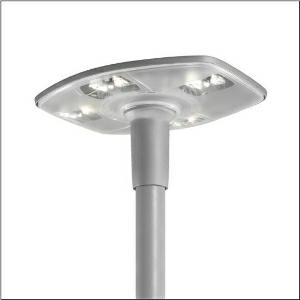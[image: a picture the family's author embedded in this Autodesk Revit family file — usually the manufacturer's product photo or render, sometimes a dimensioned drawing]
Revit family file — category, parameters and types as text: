
# Revit family: dl_r__30_led___st1_2c_5xa513271b08a5_992b
name_source: partatom
category: Lighting Fixtures
units: mm (PartAtom-declared; Revit-internal decimal feet)

## family parameters
Cut with Voids When Loaded = No
Host = Face
Light Source = No
Part Type = Normal
Room Calculation Point = No
Round Connector Dimension = Use Diameter
Shared = No

## types (1)
- --- (1 x LED, 5540 lm, 48.9 W, 4000K)
    Apparent Load = 49 VA
    CIE Flux Codes = 32 71 98 100 100
    Color Rendering = 70
    Color Temperature = 4000K
    Default Elevation = 1800 mm
    Description = DL® 30 LED, mast luminaire, primary light control with 3 zone facetted reflector, of plastic, aluminium vaporised, highly specular, primary optical cover: cover, of PMMA, structured, transparent, light distribution: ST1.2c, light emission: direct distribution, primary light characteristic: asymmetric, crossroads, installation type: post-top, LED, High Power LED, rated luminous flux: 5.540lm, luminous efficacy: 113lm/W, light colour: 740, colour temperature: 4000K, control gear: Plus, control: flexible luminous flux parameterisation, time-dependent luminous flux control, constant luminous flux control, digital communication interface, power reduction, electronic power reduction, mains connection: 230..240V, AC, 50/60Hz, start of lifetime: 49W, end of service life: 51W, reduction: 23W, luminaire housing, of diecast aluminium, powder-coated, Siteco® metallic grey (DB 702S), length: 600mm, width: 510mm, height: 290mm, spigot size: d x l = 76 x 100mm (post-top) | with reducer (optional accessory) 60 x 100mm, mounting height: 3..6m, protection rating (complete): IP66, insulation class (complete): insulation class II (safety insulation), certification: CE, ENEC, VDE, impact resistance: IK08, permissible operating ambient temperature: -25..+30°C, standard-compliant lighting for roads and squares, packaging unit: 1 piece

Light Distribution: ST1.2c
    Height = 290 mm
    Lamp = 1 x LED
    Lamp Light Flux = 5540 lm
    Lamp Power = 48.9 W
    Lamp count = 1
    Length = 510 mm
    Luminous efficacy = 113 lm/W
    Manufacturer = Siteco
    ModVariant = No
    Model = 5XA513271B08A5
    Number of Poles = 1
    OnlyDefault = Yes
    Power Factor = 1
    Product Name = DL® 30 LED | ST1.2c
    Product group = mast luminaire | pylon top
    ProductGroupID = 6100
    Protection Class = Protection class II
    Protection Degree = IP 66
    RLX_Detail_Level = 1
    RLX_Emergency_Light_Flux = 0 lm
    RLX_Emergency_Type = 0
    RLX_Emergency_Type_DB = No
    RlxData = <blob elided: 86469 chars, md5=4ec51665>
    Socket = socket
    Standby Power = 0 W
    System Light Flux = 5540 lm
    System Power = 49 W
    Type Comments = factory setting: luminous flux: 100 % | dim-lin: 254 | 497 mA
    Type Image = l_1006003.jpg
    URL = http://relux.com
    VarID = @adj_219181
    Voltage = 0 V
    Weight = 0.00 kg
    Width = 600 mm

## geometry (parser evidence)
native form markers: Blend x4, Sweep x11
no freeform markers — native parametric forms only
